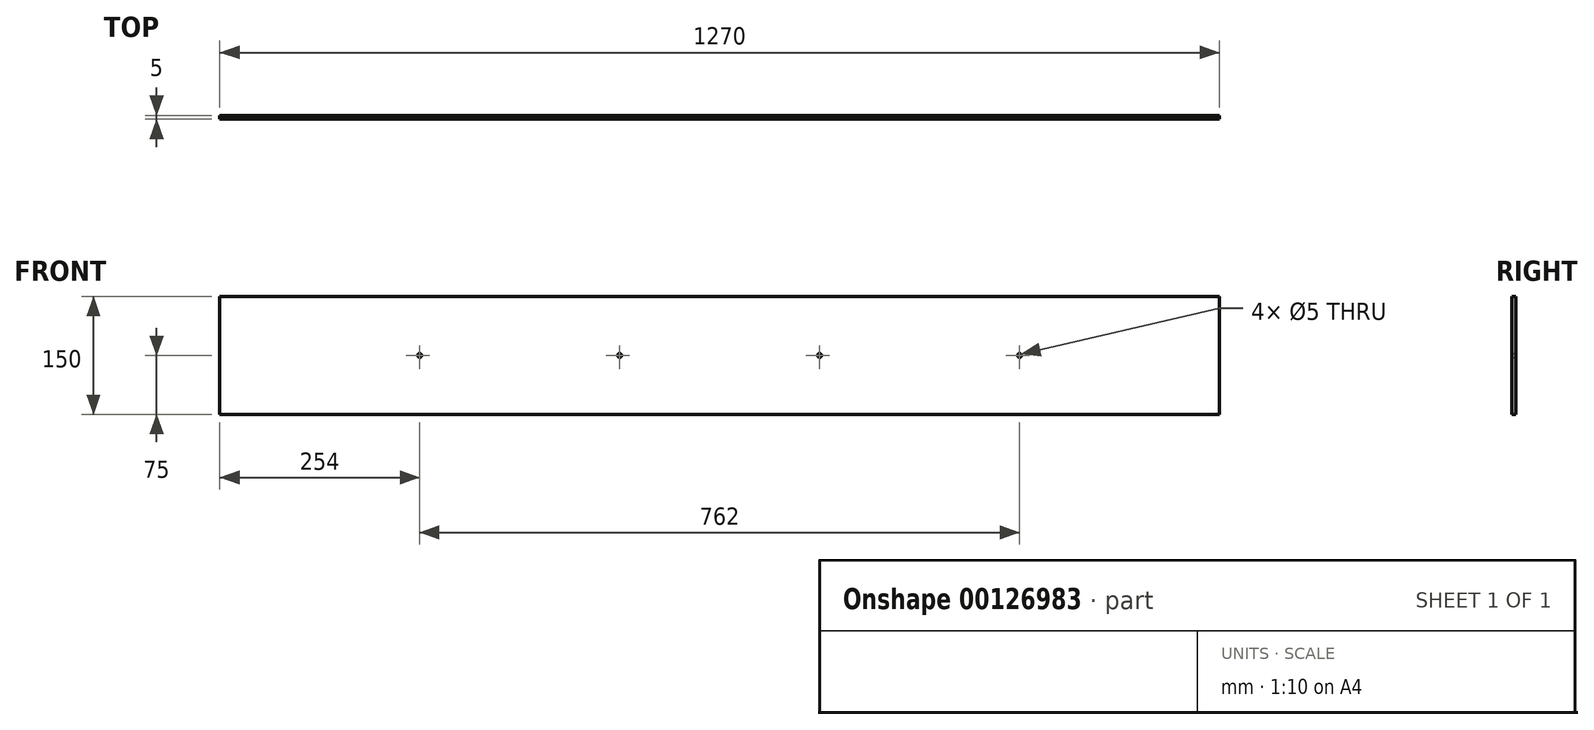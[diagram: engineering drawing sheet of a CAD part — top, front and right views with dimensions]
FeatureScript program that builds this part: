
annotation { "Feature Type Name" : "Feature", "Feature Type Description" : "" }
export const myFeature = defineFeature(function(context is Context, id is Id, definition is map)
    precondition{}
    {
        {
            var Q0;
            Q0=qCreatedBy(makeId("Front.planeOp"),FACE);
            var sketch = newSketch(context, id + "F0", { "sketchPlane" : qUnion([Q0])});
            skLineSegment(sketch, "E0.bottom", {"start": v(0, 0) * mm, "end": v(1270, 0) * mm});
            skLineSegment(sketch, "E0.top", {"start": v(0, 150) * mm, "end": v(1270, 150) * mm});
            skLineSegment(sketch, "E0.left", {"start": v(0, 0) * mm, "end": v(0, 150) * mm});
            skLineSegment(sketch, "E0.right", {"start": v(1270, 0) * mm, "end": v(1270, 150) * mm});
            skCircle(sketch, "E1", {"center": v(254, 75) * mm, "radius": 2.5 * mm});
            skPoint(sketch, "E1.centerSnap0", {"position": v(0, 75) * mm});
            skCircle(sketch, "E2.1.0.0", {"center": v(508, 75) * mm, "radius": 2.5 * mm});
            skCircle(sketch, "E2.2.0.0", {"center": v(762, 75) * mm, "radius": 2.5 * mm});
            skCircle(sketch, "E2.3.0.0", {"center": v(1016, 75) * mm, "radius": 2.5 * mm});
            skLineSegment(sketch, "E2.direction1", {"start": v(254, 75) * mm, "end": v(508, 75) * mm, "construction": true});
            skSolve(sketch);
        }
        {
            var Q0;
            Q0=makeQuery(id+"F0.imprint","IMPRINT",FACE,{"disambiguationData":[TD([[makeQuery(id+"F0.imprint","IMPRINT",EDGE,{"derivedFrom":sQuery(id+"F0.wireOp",EDGE,"E0.bottom")}),1.0]])]});
            extrude(context, id + "F1", {"entities" : qUnion([Q0]), "depth" : 5 * mm});
        }
    });
